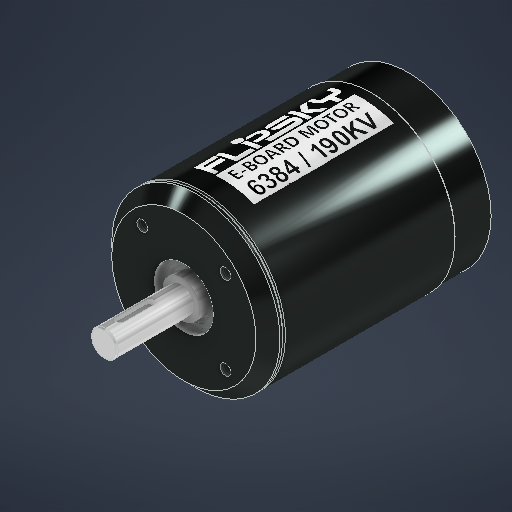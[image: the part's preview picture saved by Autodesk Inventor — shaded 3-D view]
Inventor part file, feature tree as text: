
AUTODESK INVENTOR PART (.ipt)
format: ipt  version: 2025 (Build 290162000, 162)  size: 801,280 bytes
history: native  units: in
note: dims shown in document units (in); Inventor stores cm internally (conversion verified against a paired STEP export)
features: sketch x10, extrude x9, thread x4, chamfer x2, plane x2, other x2, revolve x1, fillet x1
ambient origin geometry x8: Origin, YZ Plane, XZ Plane, XY Plane, X Axis, Y Axis, Z Axis, Center Point
bodies: Solid1 (feature_tree)
feature tree (31):
  revolve  "Revolution1"  [1 undecoded]
  extrude  "Extrusion1"  Depth=0.0394in
  thread  "Thread1"  [1 undecoded]
  thread  "Thread2"  [1 undecoded]
  thread  "Thread3"  [1 undecoded]
  thread  "Thread4"  [1 undecoded]
  extrude  "Extrusion2"  Depth=0.1575in
  chamfer  "Chamfer1"  Distance=1.5748in Angle=360.0deg
  plane  "Work Plane1"
  extrude  "Extrusion3"  Depth=0.3937in TaperAngle=0.0deg
  plane  "Work Plane2"
  other  "Decal1"
  extrude  "Extrusion4"  Depth=0.3937in TaperAngle=0.0deg
  chamfer  "Chamfer2"  Distance=0.3937in
  extrude  "Extrusion5"  Depth=1.1811in TaperAngle=0.0deg
  extrude  "Extrusion6"  Depth=0.1969in
  sketch  "Sketch9"  dims[d35=0.4331in d36=0.1181in d37=0.1575in d38=0.0591in d39=0.0in d40=1.4173in d52=0.0197in d53=0.5512in d54=0.0in d55=0.0197in d56=0.0787in d57=45.0deg d58=0.8661in d59=0.1181in d60=0.0in d61=0.5512in d62=0.1575in d63=0.0in d64=0.0197in d65=0.0276in d66=0.0394in d67=0.0197in d68=0.0in d69=0.0157in d70=0.0295in d71=0.0197in d72=0.0in d73=0.0138in d74=0.0197in d75=0.0in]
  extrude  "Extrusion7"  Depth=0.1181in
  extrude  "Extrusion8"  Depth=0.1575in
  fillet  "Fillet1"  Radius=0.0591in
  extrude  "Extrusion9"  Depth=0.0197in
  sketch  "Sketch1"  dims[d0=1.063in d1=1.2402in]
  sketch  "Sketch2"  dims[d10=90.0deg d11=0.1575in]
  sketch  "Sketch Circular Pattern1"  dims[d2=45.0deg d5=0.0394in d6=0.0394in d7=0.0394in d8=0.0394in d9=3.3071in]
  sketch  "Sketch3"  dims[d12=0.8661in]
  sketch  "Sketch4"  dims[d13=45.0deg d14=1.5748in d16=360.0deg]
  sketch  "Sketch5"  dims[d18=0.1969in d19=0.0in d20=0.3937in d21=0.0in]
  other  "Image1"
  sketch  "Sketch6"  dims[d22=0.3937in d23=0.0in d24=0.3937in d25=0.0in d26=0.3937in d27=0.0in]
  sketch  "Sketch7"  dims[d28=0.3937in d29=1.1811in d30=0.0in]
  sketch  "Sketch8"  dims[d31=0.0197in d32=0.0787in d33=45.0deg d34=0.1969in]
note: 5 required parameter values undecoded (feature->parameter linkage not recoverable at this tier; creation-order binding heuristic only, values carry confidence <= 0.55)